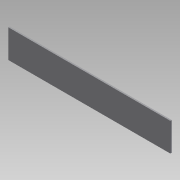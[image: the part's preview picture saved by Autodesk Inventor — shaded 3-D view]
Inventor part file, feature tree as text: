
AUTODESK INVENTOR PART (.ipt)
format: ipt  version: 2012 (Build 160160000, 160)  size: 65,024 bytes
history: native  units: in
note: dims shown in document units (in); Inventor stores cm internally (conversion verified against a paired STEP export)
features: extrude x1, sketch x1
ambient origin geometry x8: Origin, YZ Plane, XZ Plane, XY Plane, X Axis, Y Axis, Z Axis, Center Point
bodies: Solid1 (feature_tree)
feature tree (2):
  extrude  "Extrusion1"  Depth=5.0in
  sketch  "Sketch1"  dims[d0=28.628in d1=5.0in d2=0.25in d3=0.0in]
